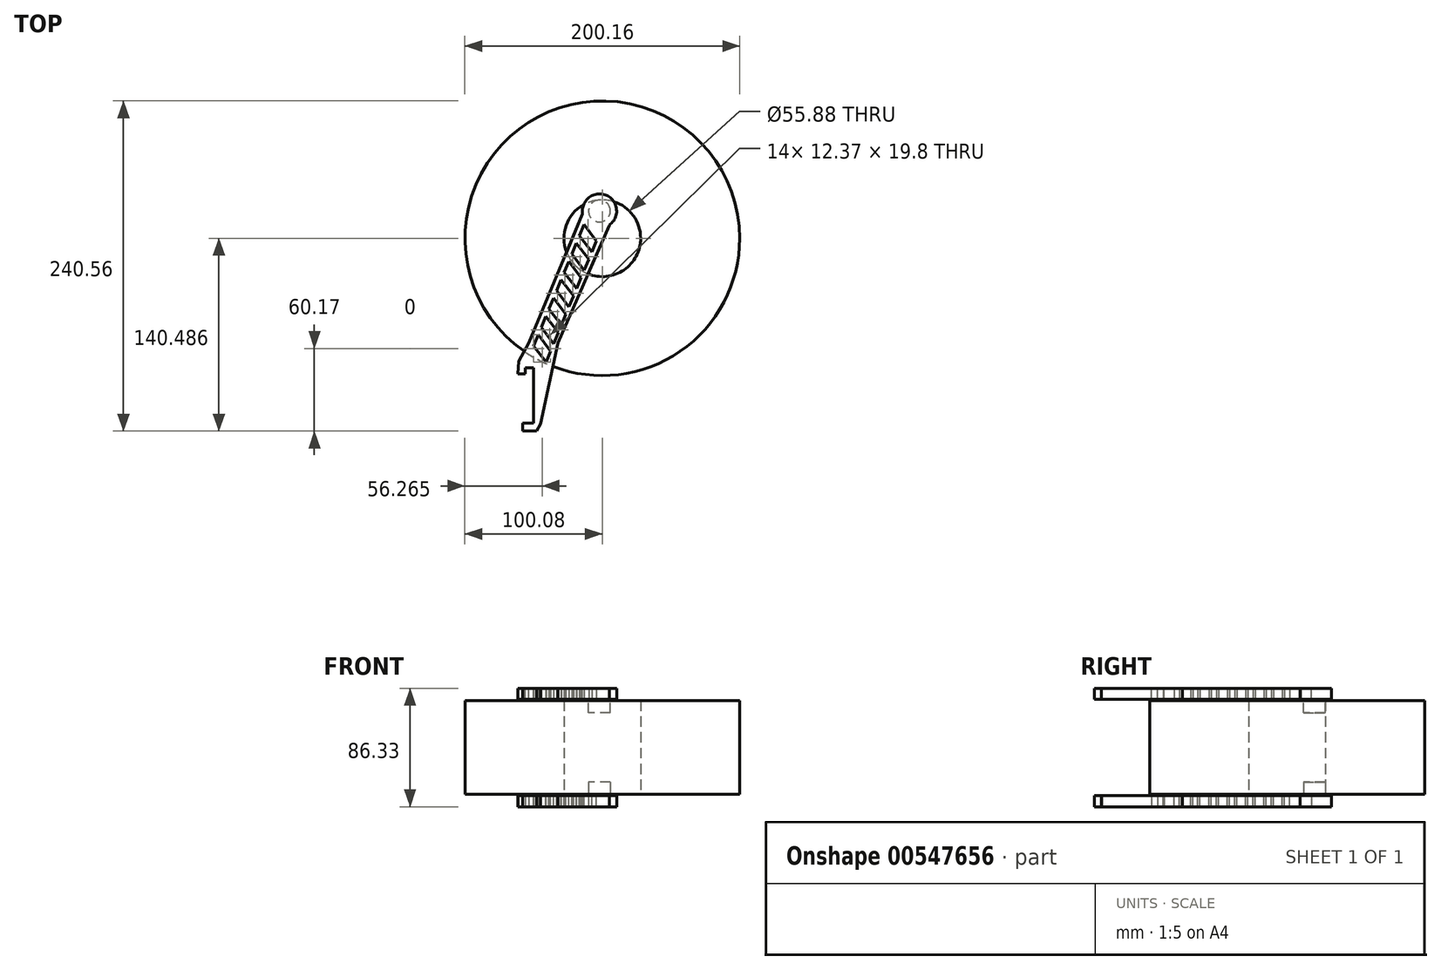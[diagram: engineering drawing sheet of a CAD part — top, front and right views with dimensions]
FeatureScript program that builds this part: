
annotation { "Feature Type Name" : "Feature", "Feature Type Description" : "" }
export const myFeature = defineFeature(function(context is Context, id is Id, definition is map)
    precondition{}
    {
        {
            var Q0;
            Q0=qCreatedBy(makeId("Top.planeOp"),FACE);
            var sketch = newSketch(context, id + "F0", { "sketchPlane" : qUnion([Q0])});
            skCircle(sketch, "E0", {"center": v(0, 23) * mm, "radius": 100 * mm, "construction": true});
            skCircle(sketch, "E1", {"center": v(0, 23) * mm, "radius": 25 * mm, "construction": true});
            skLineSegment(sketch, "E2", {"start": v(-50, -77) * mm, "end": v(-56.2, -77) * mm});
            skLineSegment(sketch, "E3", {"start": v(-56.2, -77) * mm, "end": v(-56.2, -117.1) * mm});
            skLineSegment(sketch, "E4", {"start": v(-56.2, -117.1) * mm, "end": v(-50, -117.1) * mm});
            skLineSegment(sketch, "E5", {"start": v(-50, -117.1) * mm, "end": v(-50, -77) * mm});
            skLineSegment(sketch, "E6", {"start": v(-58, -117.1) * mm, "end": v(-50, -117.1) * mm});
            skLineSegment(sketch, "E7", {"start": v(-58, -117.1) * mm, "end": v(-58, -123) * mm});
            skLineSegment(sketch, "E8", {"start": v(-58, -123) * mm, "end": v(-48, -123) * mm});
            skLineSegment(sketch, "E9", {"start": v(-48, -123) * mm, "end": v(-45, -118) * mm});
            skLineSegment(sketch, "E10", {"start": v(-61, -72) * mm, "end": v(-61.6, -81.3) * mm});
            skLineSegment(sketch, "E11", {"start": v(-61.6, -81.3) * mm, "end": v(-56.2, -81.3) * mm});
            skLineSegment(sketch, "E12", {"start": v(-56.2, -81.3) * mm, "end": v(-56.2, -77) * mm});
            skLineSegment(sketch, "E13", {"start": v(-56.2, -77) * mm, "end": v(-50, -77) * mm});
            skLineSegment(sketch, "E14", {"start": v(-50, -77) * mm, "end": v(-50, -117.1) * mm});
            skLineSegment(sketch, "E15", {"start": v(-53.48, -58.88) * mm, "end": v(-14.39, 35.3) * mm});
            skLineSegment(sketch, "E16", {"start": v(-45, -118) * mm, "end": v(-32.15, -58.86) * mm});
            skLineSegment(sketch, "E17", {"start": v(-32.15, -58.86) * mm, "end": v(5, 27) * mm});
            skArc(sketch, "E18", {"start": v(5, 27) * mm, "mid": v(2.87, 48.81) * mm, "end": v(-14.39, 35.3) * mm});
            skLineSegment(sketch, "E19", {"start": v(-53.48, -58.88) * mm, "end": v(-61, -72) * mm});
            skSolve(sketch);
        }
        {
            var Q0;
            {var subQ3=sQuery(id+"F0.wireOp",EDGE,"E7");Q0=makeQuery(id+"F0.imprint","IMPRINT",FACE,{"disambiguationData":[TD([[makeQuery(id+"F0.imprint","IMPRINT",EDGE,{"derivedFrom":subQ3}),1.0]])]});}
            extrude(context, id + "F1", {"entities" : qUnion([Q0]), "depth" : 8 * mm});
        }
        {
            var Q0;
            Q0=makeQuery(id+"F1.opExtrude","CAP_FACE",FACE,{"disambiguationData":[OSD([sQuery(id+"F0.wireOp",EDGE,"E6"),sQuery(id+"F0.wireOp",EDGE,"E7"),sQuery(id+"F0.wireOp",EDGE,"E8"),sQuery(id+"F0.wireOp",EDGE,"E9"),sQuery(id+"F0.wireOp",EDGE,"E10"),sQuery(id+"F0.wireOp",EDGE,"E11"),sQuery(id+"F0.wireOp",EDGE,"E12"),sQuery(id+"F0.wireOp",EDGE,"E13"),sQuery(id+"F0.wireOp",EDGE,"E14"),sQuery(id+"F0.wireOp",EDGE,"E15"),sQuery(id+"F0.wireOp",EDGE,"E16"),sQuery(id+"F0.wireOp",EDGE,"E17"),sQuery(id+"F0.wireOp",EDGE,"E18"),sQuery(id+"F0.wireOp",EDGE,"E19")])],"isStart":false});
            var sketch = newSketch(context, id + "F2", { "sketchPlane" : qUnion([Q0])});
            skCircle(sketch, "E20", {"center": v(-2.05, 37.32) * mm, "radius": 8 * mm});
            skSolve(sketch);
        }
        {
            var Q0;
            Q0=qSketchRegion(id+"F2",true);
            extrude(context, id + "F3", {"entities" : qUnion([Q0]), "operationType" : NewBodyOperationType.ADD, "depth" : 10 * mm});
        }
        {
            var Q0;
            Q0=makeQuery(id+"F1.opExtrude","CAP_FACE",FACE,{"disambiguationData":[OSD([sQuery(id+"F0.wireOp",EDGE,"E6"),sQuery(id+"F0.wireOp",EDGE,"E7"),sQuery(id+"F0.wireOp",EDGE,"E8"),sQuery(id+"F0.wireOp",EDGE,"E9"),sQuery(id+"F0.wireOp",EDGE,"E10"),sQuery(id+"F0.wireOp",EDGE,"E11"),sQuery(id+"F0.wireOp",EDGE,"E12"),sQuery(id+"F0.wireOp",EDGE,"E13"),sQuery(id+"F0.wireOp",EDGE,"E14"),sQuery(id+"F0.wireOp",EDGE,"E15"),sQuery(id+"F0.wireOp",EDGE,"E16"),sQuery(id+"F0.wireOp",EDGE,"E17"),sQuery(id+"F0.wireOp",EDGE,"E18"),sQuery(id+"F0.wireOp",EDGE,"E19")])],"isStart":false});
            var sketch = newSketch(context, id + "F4", { "sketchPlane" : qUnion([Q0])});
            skLineSegment(sketch, "E21", {"start": v(-16.65, 19.43) * mm, "end": v(-13.33, 27.43) * mm});
            skLineSegment(sketch, "E22", {"start": v(-13.33, 27.43) * mm, "end": v(-4.28, 15.62) * mm});
            skLineSegment(sketch, "E23", {"start": v(-4.28, 15.62) * mm, "end": v(-7.6, 7.62) * mm});
            skLineSegment(sketch, "E24", {"start": v(-7.6, 7.62) * mm, "end": v(-16.65, 19.43) * mm});
            skLineSegment(sketch, "E25.1.0.0", {"start": v(-13.16, -5.77) * mm, "end": v(-22.2, 6.04) * mm});
            skLineSegment(sketch, "E25.1.0.1", {"start": v(-18.89, 14.03) * mm, "end": v(-9.84, 2.23) * mm});
            skLineSegment(sketch, "E25.1.0.2", {"start": v(-22.2, 6.04) * mm, "end": v(-18.89, 14.03) * mm});
            skLineSegment(sketch, "E25.1.0.3", {"start": v(-9.84, 2.23) * mm, "end": v(-13.16, -5.77) * mm});
            skLineSegment(sketch, "E25.2.0.0", {"start": v(-18.72, -19.16) * mm, "end": v(-27.76, -7.36) * mm});
            skLineSegment(sketch, "E25.2.0.1", {"start": v(-24.44, 0.64) * mm, "end": v(-15.4, -11.16) * mm});
            skLineSegment(sketch, "E25.2.0.2", {"start": v(-27.76, -7.36) * mm, "end": v(-24.44, 0.64) * mm});
            skLineSegment(sketch, "E25.2.0.3", {"start": v(-15.4, -11.16) * mm, "end": v(-18.72, -19.16) * mm});
            skLineSegment(sketch, "E25.3.0.0", {"start": v(-24.28, -32.55) * mm, "end": v(-33.32, -20.75) * mm});
            skLineSegment(sketch, "E25.3.0.1", {"start": v(-30, -12.75) * mm, "end": v(-20.96, -24.56) * mm});
            skLineSegment(sketch, "E25.3.0.2", {"start": v(-33.32, -20.75) * mm, "end": v(-30, -12.75) * mm});
            skLineSegment(sketch, "E25.3.0.3", {"start": v(-20.96, -24.56) * mm, "end": v(-24.28, -32.55) * mm});
            skLineSegment(sketch, "E25.4.0.0", {"start": v(-29.84, -45.95) * mm, "end": v(-38.88, -34.14) * mm});
            skLineSegment(sketch, "E25.4.0.1", {"start": v(-35.56, -26.14) * mm, "end": v(-26.52, -37.95) * mm});
            skLineSegment(sketch, "E25.4.0.2", {"start": v(-38.88, -34.14) * mm, "end": v(-35.56, -26.14) * mm});
            skLineSegment(sketch, "E25.4.0.3", {"start": v(-26.52, -37.95) * mm, "end": v(-29.84, -45.95) * mm});
            skLineSegment(sketch, "E25.5.0.0", {"start": v(-35.4, -59.34) * mm, "end": v(-44.44, -47.53) * mm});
            skLineSegment(sketch, "E25.5.0.1", {"start": v(-41.12, -39.54) * mm, "end": v(-32.07, -51.34) * mm});
            skLineSegment(sketch, "E25.5.0.2", {"start": v(-44.44, -47.53) * mm, "end": v(-41.12, -39.54) * mm});
            skLineSegment(sketch, "E25.5.0.3", {"start": v(-32.07, -51.34) * mm, "end": v(-35.4, -59.34) * mm});
            skLineSegment(sketch, "E25.6.0.0", {"start": v(-40.95, -72.73) * mm, "end": v(-50, -60.93) * mm});
            skLineSegment(sketch, "E25.6.0.1", {"start": v(-46.68, -52.93) * mm, "end": v(-37.63, -64.73) * mm});
            skLineSegment(sketch, "E25.6.0.2", {"start": v(-50, -60.93) * mm, "end": v(-46.68, -52.93) * mm});
            skLineSegment(sketch, "E25.6.0.3", {"start": v(-37.63, -64.73) * mm, "end": v(-40.95, -72.73) * mm});
            skLineSegment(sketch, "E25.direction1", {"start": v(-7.6, 7.62) * mm, "end": v(-13.16, -5.77) * mm, "construction": true});
            skSolve(sketch);
        }
        {
            var Q0;
            Q0=qSketchRegion(id+"F4",true);
            extrude(context, id + "F5", {"entities" : qUnion([Q0]), "operationType" : NewBodyOperationType.REMOVE, "endBound" : BoundingType.THROUGH_ALL, "oppositeDirection" : true, "depth" : 25 * mm});
        }
        {
            var Q0;
            Q0=makeQuery(id+"F1.opExtrude","SWEPT_BODY",BODY,{"disambiguationData":[OSD([sQuery(id+"F0.wireOp",EDGE,"E6"),sQuery(id+"F0.wireOp",EDGE,"E7"),sQuery(id+"F0.wireOp",EDGE,"E8"),sQuery(id+"F0.wireOp",EDGE,"E9"),sQuery(id+"F0.wireOp",EDGE,"E10"),sQuery(id+"F0.wireOp",EDGE,"E11"),sQuery(id+"F0.wireOp",EDGE,"E12"),sQuery(id+"F0.wireOp",EDGE,"E13"),sQuery(id+"F0.wireOp",EDGE,"E14"),sQuery(id+"F0.wireOp",EDGE,"E15"),sQuery(id+"F0.wireOp",EDGE,"E16"),sQuery(id+"F0.wireOp",EDGE,"E17"),sQuery(id+"F0.wireOp",EDGE,"E18"),sQuery(id+"F0.wireOp",EDGE,"E19")])]});
            var Q1;
            Q1=qCreatedBy(makeId("Top.planeOp"),FACE);
            mirror(context, id + "F6", {"entities" : qUnion([Q0]), "mirrorPlane" : qUnion([Q1])});
        }
        {
            var Q0;
            Q0=makeQuery(id+"F1.opExtrude","CAP_FACE",FACE,{"disambiguationData":[OSD([sQuery(id+"F0.wireOp",EDGE,"E6"),sQuery(id+"F0.wireOp",EDGE,"E7"),sQuery(id+"F0.wireOp",EDGE,"E8"),sQuery(id+"F0.wireOp",EDGE,"E9"),sQuery(id+"F0.wireOp",EDGE,"E10"),sQuery(id+"F0.wireOp",EDGE,"E11"),sQuery(id+"F0.wireOp",EDGE,"E12"),sQuery(id+"F0.wireOp",EDGE,"E13"),sQuery(id+"F0.wireOp",EDGE,"E14"),sQuery(id+"F0.wireOp",EDGE,"E15"),sQuery(id+"F0.wireOp",EDGE,"E16"),sQuery(id+"F0.wireOp",EDGE,"E17"),sQuery(id+"F0.wireOp",EDGE,"E18"),sQuery(id+"F0.wireOp",EDGE,"E19")])],"isStart":false});
            var sketch = newSketch(context, id + "F7", { "sketchPlane" : qUnion([Q0])});
            skCircle(sketch, "E26", {"center": v(0, 17.49) * mm, "radius": 27.94 * mm});
            skCircle(sketch, "E27", {"center": v(0, 17.49) * mm, "radius": 100.08 * mm});
            skSolve(sketch);
        }
        {
            var Q0;
            Q0=makeQuery(id+"F7.imprint","IMPRINT",FACE,{"disambiguationData":[TD([[makeQuery(id+"F7.imprint","IMPRINT",EDGE,{"derivedFrom":makeQuery(id+"F1.opExtrude","CAP_EDGE",EDGE,{"disambiguationData":[OSD([sQuery(id+"F0.wireOp",EDGE,"E6")])],"isStart":false})}),-1.0]])]});
            cPlane(context, id + "F8", {"entities" : qUnion([Q0]), "cplaneType" : CPlaneType.OFFSET, "offset" : 1 * mm, "width" : 150 * mm, "height" : 150 * mm});
        }
        {
            var Q0;
            Q0=qCreatedBy(id+"F8.planeOp",FACE);
            var sketch = newSketch(context, id + "F9", { "sketchPlane" : qUnion([Q0])});
            skCircle(sketch, "E28.0", {"center": v(0, 17.49) * mm, "radius": 27.94 * mm});
            skCircle(sketch, "E28.1", {"center": v(0, 17.49) * mm, "radius": 100.08 * mm});
            skSolve(sketch);
        }
        {
            var Q0;
            Q0=qSketchRegion(id+"F9",true);
            extrude(context, id + "F10", {"entities" : qUnion([Q0]), "depth" : 68.33 * mm});
        }
        {
            var Q0;
            Q0=makeQuery(id+"F6.opPattern","COPY",BODY,{"derivedFrom":makeQuery(id+"F1.opExtrude","SWEPT_BODY",BODY,{"disambiguationData":[OSD([sQuery(id+"F0.wireOp",EDGE,"E6"),sQuery(id+"F0.wireOp",EDGE,"E7"),sQuery(id+"F0.wireOp",EDGE,"E8"),sQuery(id+"F0.wireOp",EDGE,"E9"),sQuery(id+"F0.wireOp",EDGE,"E10"),sQuery(id+"F0.wireOp",EDGE,"E11"),sQuery(id+"F0.wireOp",EDGE,"E12"),sQuery(id+"F0.wireOp",EDGE,"E13"),sQuery(id+"F0.wireOp",EDGE,"E14"),sQuery(id+"F0.wireOp",EDGE,"E15"),sQuery(id+"F0.wireOp",EDGE,"E16"),sQuery(id+"F0.wireOp",EDGE,"E17"),sQuery(id+"F0.wireOp",EDGE,"E18"),sQuery(id+"F0.wireOp",EDGE,"E19")])]}),"instanceName":"1"});
            var Q1;
            Q1=makeQuery(id+"F1.opExtrude","SWEPT_EDGE",EDGE,{"disambiguationData":[OSD([sQuery(id+"F0.wireOp",EDGE,"E15"),sQuery(id+"F0.wireOp",EDGE,"E18")])]});
            transform(context, id + "F11", {"entities" : qUnion([Q0]), "transformType" : TransformType.TRANSLATION_DISTANCE, "transformDirection" : qUnion([Q1]), "distance" : 86.33 * mm, "oppositeDirection" : true, "makeCopy" : false});
        }
    });
